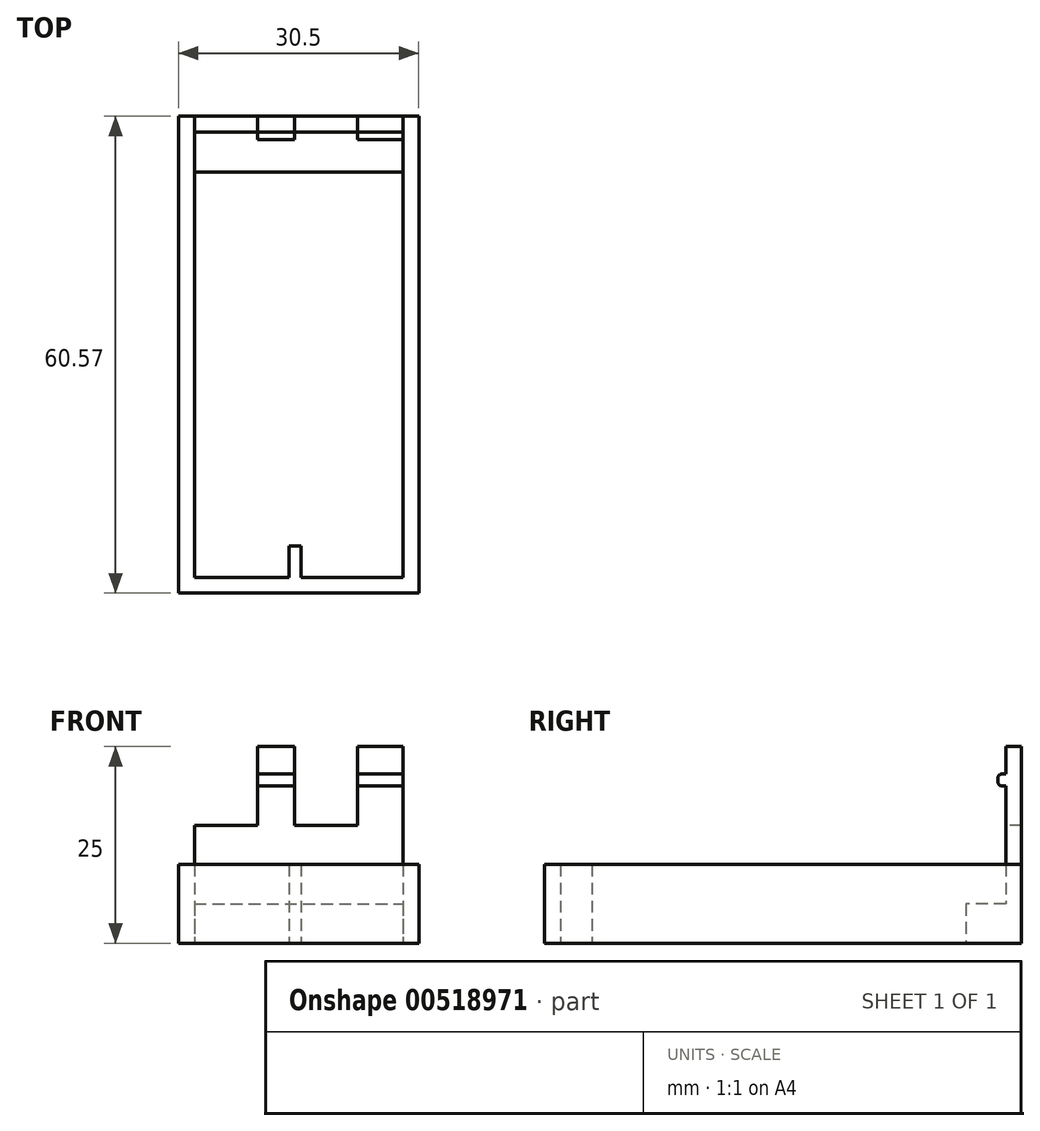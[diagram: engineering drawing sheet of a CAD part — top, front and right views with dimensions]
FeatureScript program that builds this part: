
annotation { "Feature Type Name" : "Feature", "Feature Type Description" : "" }
export const myFeature = defineFeature(function(context is Context, id is Id, definition is map)
    precondition{}
    {
        {
            var Q0;
            Q0=qCreatedBy(makeId("Top.planeOp"),FACE);
            var sketch = newSketch(context, id + "F0", { "sketchPlane" : qUnion([Q0])});
            skLineSegment(sketch, "E0.bottom", {"start": v(-12.89, 32.53) * mm, "end": v(13.61, 32.53) * mm});
            skLineSegment(sketch, "E0.top", {"start": v(-12.89, -24.04) * mm, "end": v(13.61, -24.04) * mm});
            skLineSegment(sketch, "E0.left", {"start": v(-12.89, 32.53) * mm, "end": v(-12.89, -24.04) * mm});
            skLineSegment(sketch, "E0.right", {"start": v(13.61, 32.53) * mm, "end": v(13.61, -24.04) * mm});
            skLineSegment(sketch, "E1.bottom", {"start": v(-14.89, 34.53) * mm, "end": v(15.61, 34.53) * mm});
            skLineSegment(sketch, "E1.top", {"start": v(-14.89, -26.04) * mm, "end": v(15.61, -26.04) * mm});
            skLineSegment(sketch, "E1.left", {"start": v(-14.89, 34.53) * mm, "end": v(-14.89, -26.04) * mm});
            skLineSegment(sketch, "E1.right", {"start": v(15.61, 34.53) * mm, "end": v(15.61, -26.04) * mm});
            skLineSegment(sketch, "E2", {"start": v(-12.89, -5.22) * mm, "end": v(-14.89, -5.22) * mm, "construction": true});
            skLineSegment(sketch, "E3", {"start": v(3.46, -24.04) * mm, "end": v(3.46, -26.04) * mm, "construction": true});
            skLineSegment(sketch, "E4", {"start": v(13.61, -8.08) * mm, "end": v(15.61, -8.08) * mm, "construction": true});
            skLineSegment(sketch, "E5.top", {"start": v(-12.89, 27.46) * mm, "end": v(13.61, 27.46) * mm});
            skLineSegment(sketch, "E5.left", {"start": v(-12.89, 32.53) * mm, "end": v(-12.89, 27.46) * mm});
            skLineSegment(sketch, "E5.right", {"start": v(13.61, 32.53) * mm, "end": v(13.61, 27.46) * mm});
            skLineSegment(sketch, "E6", {"start": v(-0.89, -24.04) * mm, "end": v(-0.89, -20.04) * mm});
            skLineSegment(sketch, "E7", {"start": v(-0.89, -20.04) * mm, "end": v(0.64, -20.04) * mm});
            skLineSegment(sketch, "E8", {"start": v(0.64, -20.04) * mm, "end": v(0.64, -24.04) * mm});
            skSolve(sketch);
        }
        {
            var Q0;
            Q0=makeQuery(id+"F0.imprint","IMPRINT",FACE,{"disambiguationData":[TD([[makeQuery(id+"F0.imprint","IMPRINT",EDGE,{"derivedFrom":sQuery(id+"F0.wireOp",EDGE,"E0.top")}),-1.0]])]});
            var Q1;
            {var subQ0=sQuery(id+"F0.wireOp",EDGE,"E6");Q1=makeQuery(id+"F0.imprint","IMPRINT",FACE,{"disambiguationData":[TD([[makeQuery(id+"F0.imprint","IMPRINT",EDGE,{"derivedFrom":subQ0}),-1.0]])]});}
            extrude(context, id + "F1", {"entities" : qUnion([Q0, Q1]), "depth" : 10 * mm, "offsetDistance" : 25 * mm});
        }
        {
            var Q0;
            Q0=makeQuery(id+"F0.imprint","IMPRINT",FACE,{"disambiguationData":[TD([[makeQuery(id+"F0.imprint","IMPRINT",EDGE,{"derivedFrom":sQuery(id+"F0.wireOp",EDGE,"E0.bottom")}),-1.0]])]});
            extrude(context, id + "F2", {"entities" : qUnion([Q0]), "operationType" : NewBodyOperationType.ADD, "depth" : 5 * mm, "offsetDistance" : 25 * mm});
        }
        {
            var Q0;
            Q0=makeQuery(id+"F1.opExtrude","CAP_FACE",FACE,{"disambiguationData":[OSD([sQuery(id+"F0.wireOp",EDGE,"E0.top"),sQuery(id+"F0.wireOp",EDGE,"E0.left"),sQuery(id+"F0.wireOp",EDGE,"E0.right"),sQuery(id+"F0.wireOp",EDGE,"E1.bottom"),sQuery(id+"F0.wireOp",EDGE,"E1.top"),sQuery(id+"F0.wireOp",EDGE,"E1.left"),sQuery(id+"F0.wireOp",EDGE,"E1.right"),sQuery(id+"F0.wireOp",EDGE,"E0.bottom"),sQuery(id+"F0.wireOp",EDGE,"E5.left"),sQuery(id+"F0.wireOp",EDGE,"E5.right"),sQuery(id+"F0.wireOp",EDGE,"E6"),sQuery(id+"F0.wireOp",EDGE,"E7"),sQuery(id+"F0.wireOp",EDGE,"E8")])],"isStart":false});
            var sketch = newSketch(context, id + "F3", { "sketchPlane" : qUnion([Q0])});
            skLineSegment(sketch, "E9.bottom", {"start": v(-12.89, 32.53) * mm, "end": v(13.61, 32.53) * mm});
            skLineSegment(sketch, "E9.top", {"start": v(-12.89, 34.53) * mm, "end": v(13.61, 34.53) * mm});
            skLineSegment(sketch, "E9.left", {"start": v(-12.89, 32.53) * mm, "end": v(-12.89, 34.53) * mm});
            skLineSegment(sketch, "E9.right", {"start": v(13.61, 32.53) * mm, "end": v(13.61, 34.53) * mm});
            skSolve(sketch);
        }
        {
            var Q0;
            Q0=makeQuery(id+"F3.imprint","IMPRINT",FACE,{"disambiguationData":[TD([[makeQuery(id+"F3.imprint","IMPRINT",EDGE,{"derivedFrom":sQuery(id+"F3.wireOp",EDGE,"E9.bottom")}),1.0]])]});
            extrude(context, id + "F4", {"entities" : qUnion([Q0]), "operationType" : NewBodyOperationType.ADD, "depth" : 15 * mm, "offsetDistance" : 25 * mm});
        }
        {
            var Q0;
            Q0=makeQuery(id+"F4.opExtrude","SWEPT_FACE",FACE,{"disambiguationData":[OSD([sQuery(id+"F3.wireOp",EDGE,"E9.right")])]});
            var sketch = newSketch(context, id + "F5", { "sketchPlane" : qUnion([Q0])});
            skLineSegment(sketch, "E10.bottom", {"start": v(32.53, 21.5) * mm, "end": v(31.53, 21.5) * mm});
            skLineSegment(sketch, "E10.top", {"start": v(32.53, 20) * mm, "end": v(31.53, 20) * mm});
            skLineSegment(sketch, "E10.left", {"start": v(32.53, 21.5) * mm, "end": v(32.53, 20) * mm});
            skLineSegment(sketch, "E10.right", {"start": v(31.53, 21.5) * mm, "end": v(31.53, 20) * mm});
            skSolve(sketch);
        }
        {
            var Q0;
            Q0=makeQuery(id+"F5.imprint","IMPRINT",FACE,{"disambiguationData":[TD([[makeQuery(id+"F5.imprint","IMPRINT",EDGE,{"derivedFrom":sQuery(id+"F5.wireOp",EDGE,"E10.bottom")}),1.0]])]});
            extrude(context, id + "F6", {"entities" : qUnion([Q0]), "operationType" : NewBodyOperationType.ADD, "oppositeDirection" : true, "depth" : 25.4 * mm, "offsetDistance" : 25 * mm});
        }
        {
            var Q0;
            Q0=makeQuery(id+"F6.opExtrude","SWEPT_EDGE",EDGE,{"disambiguationData":[OSD([sQuery(id+"F5.wireOp",EDGE,"E10.bottom"),sQuery(id+"F5.wireOp",EDGE,"E10.right")])]});
            var Q1;
            Q1=makeQuery(id+"F6.opExtrude","SWEPT_EDGE",EDGE,{"disambiguationData":[OSD([sQuery(id+"F5.wireOp",EDGE,"E10.top"),sQuery(id+"F5.wireOp",EDGE,"E10.right")])]});
            fillet(context, id + "F7", {"entities" : qUnion([Q0, Q1]), "radius" : 0.5 * mm, "tangentPropagation" : true, "allowEdgeOverflow" : false});
        }
        {
            var Q0;
            Q0=makeQuery(id+"F4.opExtrude","CAP_FACE",FACE,{"disambiguationData":[OSD([sQuery(id+"F3.wireOp",EDGE,"E9.bottom"),sQuery(id+"F3.wireOp",EDGE,"E9.top"),sQuery(id+"F3.wireOp",EDGE,"E9.left"),sQuery(id+"F3.wireOp",EDGE,"E9.right")])],"isStart":false});
            var sketch = newSketch(context, id + "F8", { "sketchPlane" : qUnion([Q0])});
            skLineSegment(sketch, "E11.bottom", {"start": v(-12.89, 34.53) * mm, "end": v(-4.89, 34.53) * mm});
            skLineSegment(sketch, "E11.top", {"start": v(-12.89, 27.38) * mm, "end": v(-4.89, 27.38) * mm});
            skLineSegment(sketch, "E11.left", {"start": v(-12.89, 34.53) * mm, "end": v(-12.89, 27.38) * mm});
            skLineSegment(sketch, "E11.right", {"start": v(-4.89, 34.53) * mm, "end": v(-4.89, 27.38) * mm});
            skLineSegment(sketch, "E12.bottom", {"start": v(-0.19, 34.53) * mm, "end": v(7.81, 34.53) * mm});
            skLineSegment(sketch, "E12.top", {"start": v(-0.19, 27.38) * mm, "end": v(7.81, 27.38) * mm});
            skLineSegment(sketch, "E12.left", {"start": v(-0.19, 34.53) * mm, "end": v(-0.19, 27.38) * mm});
            skLineSegment(sketch, "E12.right", {"start": v(7.81, 34.53) * mm, "end": v(7.81, 27.38) * mm});
            skSolve(sketch);
        }
        {
            var Q0;
            Q0 = qSketchRegion(id + "F8", true);
            extrude(context, id + "F9", {"entities" : qUnion([Q0]), "operationType" : NewBodyOperationType.REMOVE, "oppositeDirection" : true, "depth" : 10 * mm, "offsetDistance" : 25 * mm});
        }
    });
